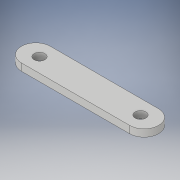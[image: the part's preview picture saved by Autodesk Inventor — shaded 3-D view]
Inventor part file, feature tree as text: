
AUTODESK INVENTOR PART (.ipt)
format: ipt  version: 2019 (Build 230136000, 136)  size: 107,520 bytes
history: native  units: mm
features: other x1, extrude x1, sketch x1
ambient origin geometry x8: Origin, YZ Plane, XZ Plane, XY Plane, X Axis, Y Axis, Z Axis, Center Point
bodies: Body1 (feature_tree)
feature tree (3):
  other  "Sólido1"
  extrude  "Extrusión1"  Depth=14.0mm
  sketch  "Boceto1"  dims[d2=3.0mm d3=3.0mm d4=14.0mm d5=0.0mm d6=0.0mm d7=28.0mm d8=4.0mm d9=15.0mm d10=2.0mm d11=0.0mm]
